# Revit family: Furniture_Table
name_source: partatom
category: Furniture
revit_build: Autodesk Revit 2014 (Build: 20130709_2115(x64)
units: mm (PartAtom-declared; Revit-internal decimal feet)

## types (14) — shared parameters
Model = 700x1500mm

## per-type parameters (varying)
| type | Length | Type Mark | Width |
| 600x1500mm | 1500 mm  [stored 4.92126 ft] | 600x1500mm | 600 mm |
| 700x1200mm | 1200 mm | 700x1200mm | 700 mm  [stored 2.29659 ft] |
| 700x1500mm | 1500 mm  [stored 4.92126 ft] | 700x1500mm | 700 mm  [stored 2.29659 ft] |
| 700x1800mm | 1800 mm  [stored 5.90551 ft] | 700x1800mm | 700 mm  [stored 2.29659 ft] |
| 500x1200mm | 1200 mm | 500x1200mm | 500 mm  [stored 1.64042 ft] |
| 500x900mm | 900 mm  [stored 2.95276 ft] | 500x900mm | 500 mm  [stored 1.64042 ft] |
| Furniture_Table | 1500 mm  [stored 4.92126 ft] | 500x1000mm | 690 mm  [stored 2.26378 ft] |
| 500x1000mm | 1000 mm  [stored 3.28084 ft] | 500x1000mm | 500 mm  [stored 1.64042 ft] |
| 550x700mm | 550 mm | 550x700mm | 700 mm  [stored 2.29659 ft] |
| 700x700mm | 700 mm  [stored 2.29659 ft] | 700x700mm | 700 mm  [stored 2.29659 ft] |
| 900x1200mm | 1200 mm | 900x1200mm | 900 mm  [stored 2.95276 ft] |
| 1000x1400mm | 1400 mm  [stored 4.59318 ft] | 1000x1400mm | 1000 mm  [stored 3.28084 ft] |
| 1400x1000mm | 1400 mm  [stored 4.59318 ft] | 1000x1400mm | 1000 mm  [stored 3.28084 ft] |
| 700x550mm | 550 mm | 700x550mm | 700 mm  [stored 2.29659 ft] |

note: [stored X ft] marks values corroborated as IEEE doubles in the binary element streams (Revit-internal decimal feet)

## geometry (parser evidence)
native form markers: Sweep x3
no freeform markers — native parametric forms only
